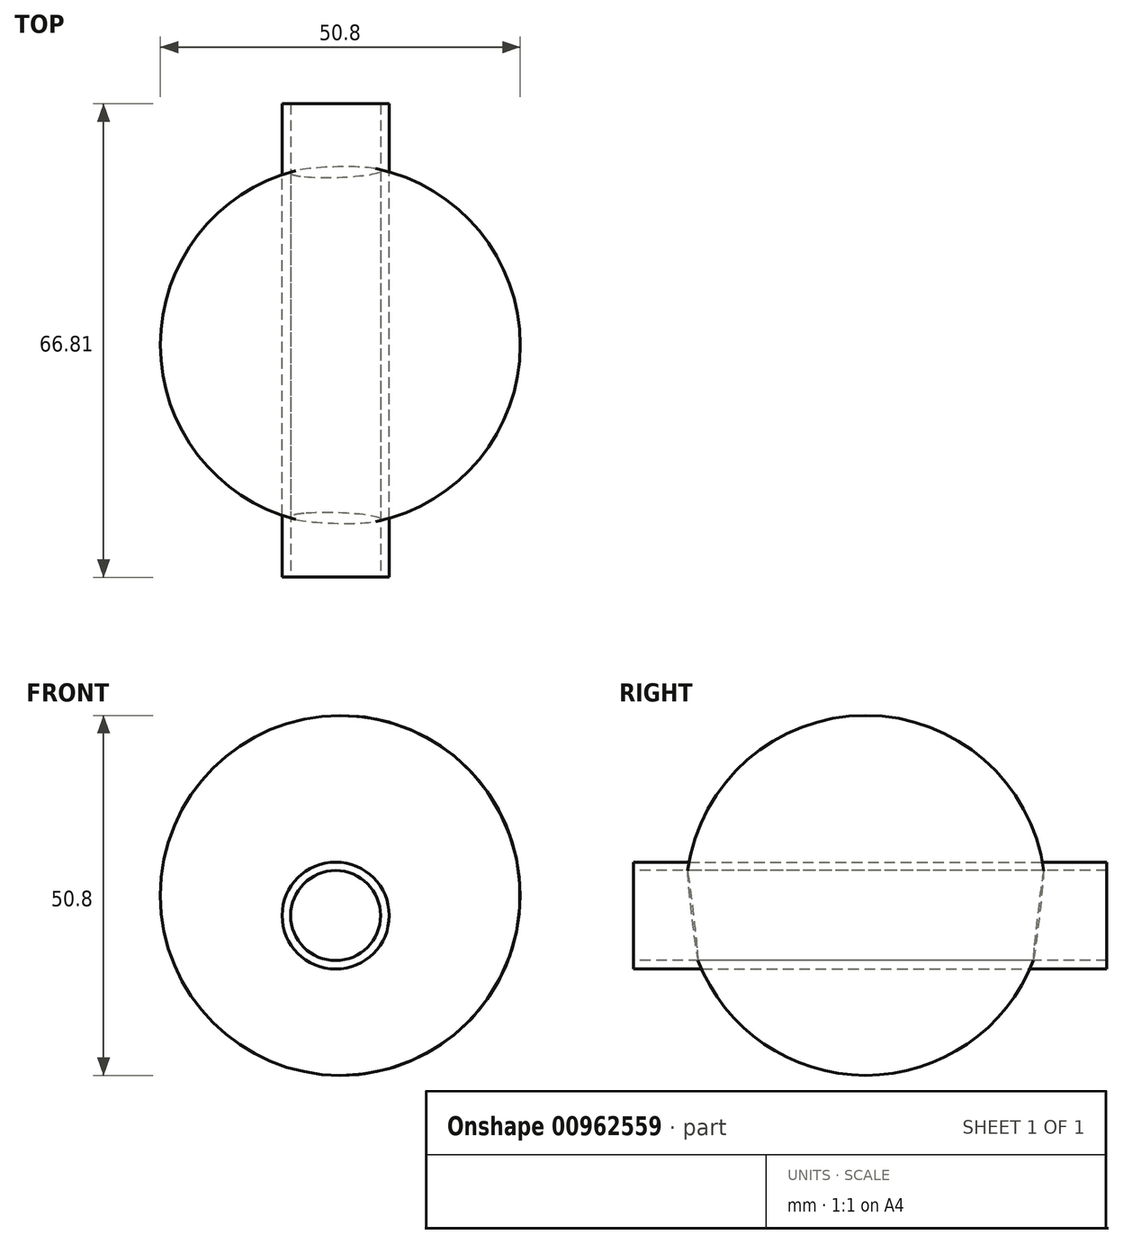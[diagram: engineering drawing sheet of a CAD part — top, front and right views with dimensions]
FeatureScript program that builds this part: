
annotation { "Feature Type Name" : "Feature", "Feature Type Description" : "" }
export const myFeature = defineFeature(function(context is Context, id is Id, definition is map)
    precondition{}
    {
        {
            var Q0;
            Q0=qCreatedBy(makeId("Front.planeOp"),FACE);
            var sketch = newSketch(context, id + "F0", { "sketchPlane" : qUnion([Q0])});
            skLineSegment(sketch, "E0", {"start": v(0, 0) * mm, "end": v(0, 50.8) * mm});
            skArc(sketch, "E1", {"start": v(0, 0) * mm, "mid": v(25.4, 25.4) * mm, "end": v(0, 50.8) * mm});
            skSolve(sketch);
        }
        {
            var Q0;
            Q0 = qSketchRegion(id + "F0", true);
            var Q1;
            Q1=sQuery(id+"F0.wireOp",EDGE,"E0");
            revolve(context, id + "F1", {"surfaceOperationType" : NewSurfaceOperationType.NEW, "entities" : qUnion([Q0]), "axis" : qUnion([Q1]), "revolveType" : RevolveType.FULL});
        }
        {
            var Q0;
            Q0=qCreatedBy(makeId("Front.planeOp"),FACE);
            var sketch = newSketch(context, id + "F2", { "sketchPlane" : qUnion([Q0])});
            skCircle(sketch, "E2", {"center": v(16.36, -18.09) * mm, "radius": 7.56 * mm});
            skSolve(sketch);
        }
        {
            var Q0;
            Q0=makeQuery(id+"F2.imprint","IMPRINT",FACE,{"disambiguationData":[TD([[makeQuery(id+"F2.imprint","IMPRINT",EDGE,{"derivedFrom":sQuery(id+"F2.wireOp",EDGE,"E2")}),1.0]])]});
            extrude(context, id + "F3", {"entities" : qUnion([Q0]), "depth" : 66.8 * mm, "offsetDistance" : 25.4 * mm});
        }
        {
            var Q0;
            Q0=makeQuery(id+"F3.opExtrude","SWEPT_BODY",BODY,{"disambiguationData":[OSD([sQuery(id+"F2.wireOp",EDGE,"E2")])]});
            transform(context, id + "F4", {"entities" : qUnion([Q0]), "transformType" : TransformType.TRANSLATION_3D, "dx" : -17.02 * mm, "dy" : 34.04 * mm, "dz" : 40.64 * mm, "makeCopy" : false});
        }
        {
            var Q0;
            Q0=makeQuery(id+"F3.opExtrude","CAP_FACE",FACE,{"disambiguationData":[OSD([sQuery(id+"F2.wireOp",EDGE,"E2")])],"isStart":false});
            var sketch = newSketch(context, id + "F5", { "sketchPlane" : qUnion([Q0])});
            skPoint(sketch, "E3", {"position": v(-0.65, 22.55) * mm});
            skSolve(sketch);
        }
        {
            var Q0;
            Q0=makeQuery(id+"F3.opExtrude","CAP_FACE",FACE,{"disambiguationData":[OSD([sQuery(id+"F2.wireOp",EDGE,"E2")])],"isStart":false});
            var Q1;
            Q1=makeQuery(id+"F3.opExtrude","CAP_FACE",FACE,{"disambiguationData":[OSD([sQuery(id+"F2.wireOp",EDGE,"E2")])],"isStart":true});
            shell(context, id + "F6", {"entities" : qUnion([Q0, Q1]), "thickness" : 2.54 * mm});
        }
        {
            var Q0;
            Q0=sQuery(id+"F5.wireOp",VERTEX,"E3");
            var Q1;
            Q1=makeQuery(id+"F3.opExtrude","SWEPT_BODY",BODY,{"disambiguationData":[OSD([sQuery(id+"F2.wireOp",EDGE,"E2")])]});
            var Q2;
            Q2=makeQuery(id+"F1.opRevolve","SWEPT_BODY",BODY,{"disambiguationData":[OSD([sQuery(id+"F0.wireOp",EDGE,"E0"),sQuery(id+"F0.wireOp",EDGE,"E1")])]});
            hole(context, id + "F7", {"style" : HoleStyle.SIMPLE, "endStyle" : HoleEndStyle.THROUGH, "holeDiameter" : 12.7 * mm, "majorDiameter" : 6.35 * mm, "isTappedThrough" : true, "tappedDepth" : 12.7 * mm, "tapClearance" : 3, "locations" : qUnion([Q0]), "scope" : qUnion([Q1, Q2])});
        }
    });
